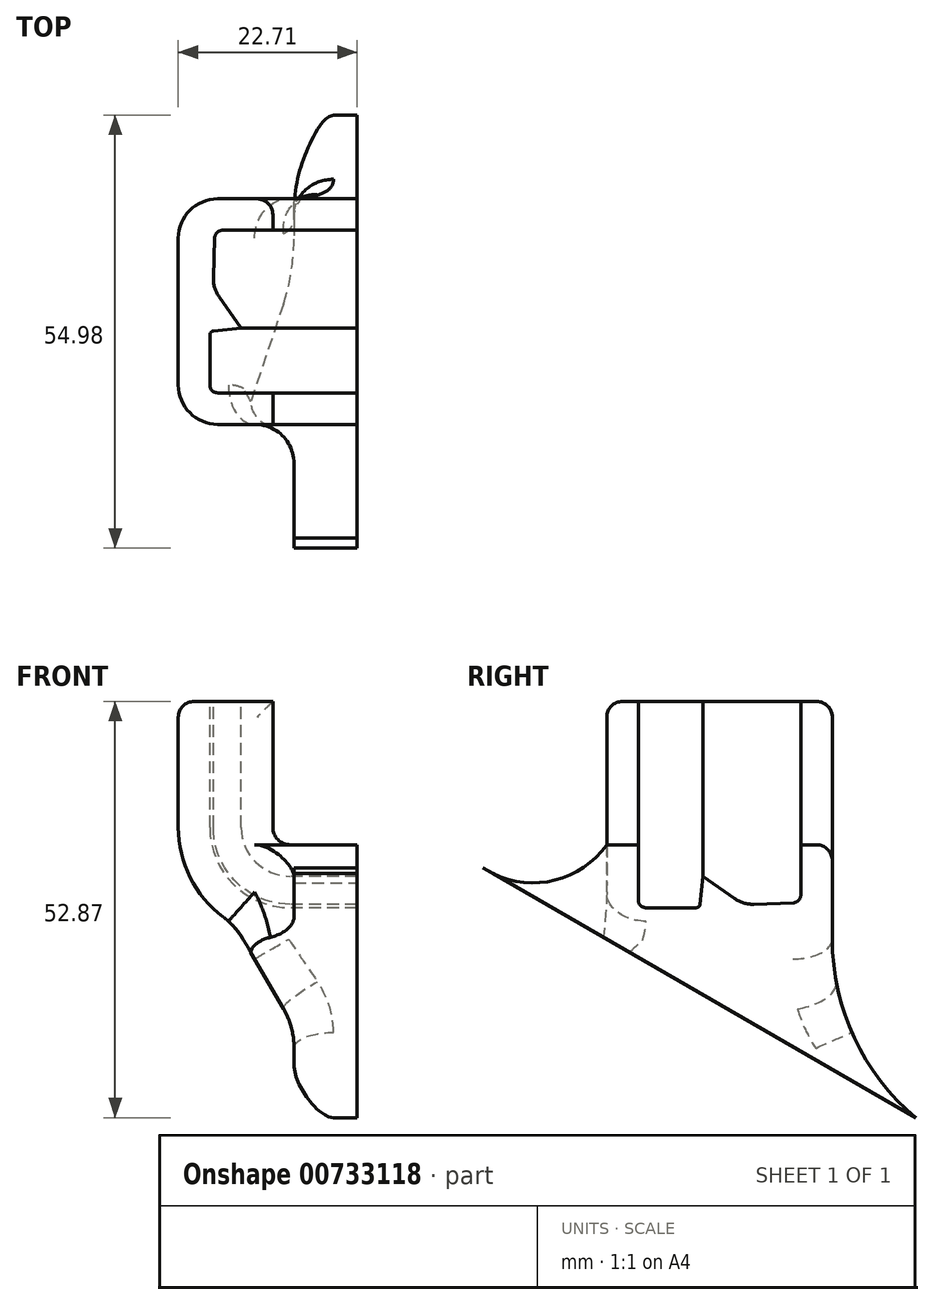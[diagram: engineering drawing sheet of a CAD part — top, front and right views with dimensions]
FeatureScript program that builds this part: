
annotation { "Feature Type Name" : "Feature", "Feature Type Description" : "" }
export const myFeature = defineFeature(function(context is Context, id is Id, definition is map)
    precondition{}
    {
        {
            var Q0;
            Q0=qCreatedBy(makeId("Front.planeOp"),FACE);
            var sketch = newSketch(context, id + "F0", { "sketchPlane" : qUnion([Q0])});
            skLineSegment(sketch, "E0", {"start": v(-73, 30.2) * mm, "end": v(-73, 14.2) * mm});
            skLineSegment(sketch, "E1", {"start": v(-58.8, 0) * mm, "end": v(0, 0) * mm});
            skPoint(sketch, "E2.visualSharp", {"position": v(-73, 0) * mm});
            skArc(sketch, "E2.filletArc", {"start": v(-73, 14.2) * mm, "mid": v(-68.84, 4.16) * mm, "end": v(-58.8, 0) * mm});
            skSolve(sketch);
        }
        {
            var Q0;
            Q0=qCreatedBy(makeId("Right.planeOp"),FACE);
            var sketch = newSketch(context, id + "F1", { "sketchPlane" : qUnion([Q0])});
            skLineSegment(sketch, "E3", {"start": v(0, 12) * mm, "end": v(4, 12) * mm});
            skLineSegment(sketch, "E4", {"start": v(4, 12) * mm, "end": v(4, 5) * mm});
            skLineSegment(sketch, "E5", {"start": v(5, 4) * mm, "end": v(11.35, 4) * mm});
            skLineSegment(sketch, "E6", {"start": v(11.85, 4.44) * mm, "end": v(12.25, 8) * mm});
            skLineSegment(sketch, "E7", {"start": v(24.65, 5.62) * mm, "end": v(24.65, 12) * mm});
            skLineSegment(sketch, "E8", {"start": v(24.65, 12) * mm, "end": v(28.65, 12) * mm});
            skLineSegment(sketch, "E9", {"start": v(28.65, 12) * mm, "end": v(28.65, 0) * mm});
            skLineSegment(sketch, "E10", {"start": v(28.65, 0) * mm, "end": v(0, 0) * mm});
            skLineSegment(sketch, "E11", {"start": v(0, 0) * mm, "end": v(0, 12) * mm});
            skLineSegment(sketch, "E12", {"start": v(12.25, 8) * mm, "end": v(16.21, 5.18) * mm});
            skPoint(sketch, "E13.visualSharp", {"position": v(16.59, 4.92) * mm});
            skPoint(sketch, "E14.visualSharp", {"position": v(4, 4) * mm});
            skArc(sketch, "E14.filletArc", {"start": v(4, 5) * mm, "mid": v(4.3, 4.3) * mm, "end": v(5, 4) * mm});
            skLineSegment(sketch, "E15", {"start": v(23.68, 4.62) * mm, "end": v(18.67, 4.45) * mm});
            skPoint(sketch, "E16.visualSharp", {"position": v(17.32, 4.4) * mm});
            skArc(sketch, "E16.filletArc", {"start": v(16.21, 5.18) * mm, "mid": v(17.38, 4.61) * mm, "end": v(18.67, 4.45) * mm});
            skPoint(sketch, "E17.visualSharp", {"position": v(24.65, 4.66) * mm});
            skArc(sketch, "E17.filletArc", {"start": v(23.68, 4.62) * mm, "mid": v(24.37, 4.93) * mm, "end": v(24.65, 5.62) * mm});
            skPoint(sketch, "E18.visualSharp", {"position": v(11.8, 4) * mm});
            skArc(sketch, "E18.filletArc", {"start": v(11.35, 4) * mm, "mid": v(11.69, 4.13) * mm, "end": v(11.85, 4.44) * mm});
            skSolve(sketch);
        }
        {
            var Q0;
            Q0 = qSketchRegion(id + "F1", true);
            var Q1;
            Q1 = qConstructionFilter(qBodyType(qCreatedBy(id + "F0" ,EDGE), BodyType.WIRE), ConstructionObject.NO);
            sweep(context, id + "F2", {"profiles" : qUnion([Q0]), "path" : qUnion([Q1])});
        }
        {
            var Q0;
            Q0=qCreatedBy(makeId("Top.planeOp"),FACE);
            var sketch = newSketch(context, id + "F3", { "sketchPlane" : qUnion([Q0])});
            skLineSegment(sketch, "E19.bottom", {"start": v(-50.3, -27.48) * mm, "end": v(2.48, -27.48) * mm});
            skLineSegment(sketch, "E19.top", {"start": v(-50.3, 55.65) * mm, "end": v(2.48, 55.65) * mm});
            skLineSegment(sketch, "E19.left", {"start": v(2.48, -27.48) * mm, "end": v(2.48, 55.65) * mm});
            skLineSegment(sketch, "E19.right", {"start": v(-50.3, -27.48) * mm, "end": v(-50.3, 55.65) * mm});
            skSolve(sketch);
        }
        {
            var Q0;
            Q0 = qSketchRegion(id + "F3", true);
            extrude(context, id + "F4", {"entities" : qUnion([Q0]), "operationType" : NewBodyOperationType.REMOVE, "depth" : 25 * mm, "offsetDistance" : 25 * mm});
        }
        {
            var Q0;
            Q0=makeQuery(id+"F4.boolean.opBoolean","COPY",FACE,{"derivedFrom":makeQuery(id+"F4.opExtrude","SWEPT_FACE",FACE,{"disambiguationData":[OSD([sQuery(id+"F3.wireOp",EDGE,"E19.right")])]})});
            var sketch = newSketch(context, id + "F5", { "sketchPlane" : qUnion([Q0])});
            skLineSegment(sketch, "E20", {"start": v(0, 0) * mm, "end": v(-15.7, 9.07) * mm});
            skLineSegment(sketch, "E21", {"start": v(0, 0) * mm, "end": v(39.27, -22.67) * mm});
            skArc(sketch, "E22", {"start": v(28.65, 0) * mm, "mid": v(31.44, -12.52) * mm, "end": v(39.27, -22.67) * mm});
            skArc(sketch, "E23", {"start": v(-15.7, 9.07) * mm, "mid": v(-7.26, 7.35) * mm, "end": v(0, 12) * mm});
            skPoint(sketch, "E23.second.point", {"position": v(0, 12) * mm});
            skPoint(sketch, "E23.third.point", {"position": v(-15.7, 28.17) * mm});
            skLineSegment(sketch, "E24", {"start": v(28.65, 0) * mm, "end": v(3.33, 0) * mm});
            skLineSegment(sketch, "E25", {"start": v(3.33, 0) * mm, "end": v(0, 12) * mm});
            skSolve(sketch);
        }
        {
            var Q0;
            Q0 = qSketchRegion(id + "F5", true);
            var Q1;
            Q1=makeQuery(id+"F2.opSweep","SWEPT_FACE",FACE,{"disambiguationData":[OSD([sQuery(id+"F0.wireOp",EDGE,"E1"),sQuery(id+"F1.wireOp",EDGE,"E3")])]});
            extrude(context, id + "F6", {"entities" : qUnion([Q0]), "operationType" : NewBodyOperationType.ADD, "oppositeDirection" : true, "depth" : 8 * mm, "endBoundEntityFace" : qUnion([Q1]), "offsetDistance" : 25 * mm});
        }
        {
            var Q0;
            Q0=makeQuery(id+"F6.boolean.opBoolean","INTERSECT",EDGE,{"derivedFrom":[makeQuery(id+"F2.opSweep","SWEPT_FACE",FACE,{"disambiguationData":[OSD([sQuery(id+"F0.wireOp",EDGE,"E1"),sQuery(id+"F1.wireOp",EDGE,"E10")])]}),makeQuery(id+"F6.opExtrude","CAP_FACE",FACE,{"disambiguationData":[OSD([sQuery(id+"F5.wireOp",EDGE,"E20"),sQuery(id+"F5.wireOp",EDGE,"E21"),sQuery(id+"F5.wireOp",EDGE,"E22"),sQuery(id+"F5.wireOp",EDGE,"E23"),sQuery(id+"F5.wireOp",EDGE,"E24"),sQuery(id+"F5.wireOp",EDGE,"E25")])],"isStart":false})]});
            chamfer(context, id + "F7", {"entities" : qUnion([Q0]), "width" : 15 * mm, "tangentPropagation" : true});
        }
        {
            var Q0;
            {var subQ0=sQuery(id+"F5.wireOp",EDGE,"E21");var subQ1=sQuery(id+"F5.wireOp",EDGE,"E20");var subQ2=sQuery(id+"F0.wireOp",EDGE,"E1");var subQ3=makeQuery(id+"F2.opSweep","SWEPT_FACE",FACE,{"disambiguationData":[OSD([subQ2,sQuery(id+"F1.wireOp",EDGE,"E10")])]});var subQ4=sQuery(id+"F5.wireOp",EDGE,"E22");var subQ5=makeQuery(id+"F6.opExtrude","CAP_FACE",FACE,{"disambiguationData":[OSD([subQ1,subQ0,subQ4,sQuery(id+"F5.wireOp",EDGE,"E23"),sQuery(id+"F5.wireOp",EDGE,"E24"),sQuery(id+"F5.wireOp",EDGE,"E25")])],"isStart":false});Q0=makeQuery(id+"F7.opChamfer","BLEND_EDGE",EDGE,{"blendedFrom":[makeQuery(id+"F6.boolean.opBoolean","INTERSECT",EDGE,{"derivedFrom":[subQ3,subQ5]}),makeQuery(id+"F6.boolean.opBoolean","SPLIT",FACE,{"disambiguationData":[TD([makeQuery(id+"F6.opExtrude","SWEPT_FACE",FACE,{"disambiguationData":[OSD([subQ4])]})])],"derivedFrom":subQ5})],"blendedInto":[makeQuery(id+"F6.boolean.opBoolean","SPLIT",FACE,{"disambiguationData":[TD([makeQuery(id+"F6.opExtrude","SWEPT_FACE",FACE,{"disambiguationData":[OSD([subQ4])]})])],"derivedFrom":subQ5})]});}
            var Q1;
            {var subQ0=sQuery(id+"F1.wireOp",EDGE,"E10");Q1=makeQuery(id+"F7.opChamfer","BLEND_EDGE",EDGE,{"blendedFrom":[makeQuery(id+"F6.boolean.opBoolean","INTERSECT",EDGE,{"derivedFrom":[makeQuery(id+"F2.opSweep","SWEPT_FACE",FACE,{"disambiguationData":[OSD([sQuery(id+"F0.wireOp",EDGE,"E1"),subQ0])]}),makeQuery(id+"F6.opExtrude","CAP_FACE",FACE,{"disambiguationData":[OSD([sQuery(id+"F5.wireOp",EDGE,"E20"),sQuery(id+"F5.wireOp",EDGE,"E21"),sQuery(id+"F5.wireOp",EDGE,"E22"),sQuery(id+"F5.wireOp",EDGE,"E23"),sQuery(id+"F5.wireOp",EDGE,"E24"),sQuery(id+"F5.wireOp",EDGE,"E25")])],"isStart":false})]}),makeQuery(id+"F2.opSweep","SWEPT_FACE",FACE,{"disambiguationData":[OSD([sQuery(id+"F0.wireOp",EDGE,"E2.filletArc"),subQ0])]})],"blendedInto":[makeQuery(id+"F2.opSweep","SWEPT_FACE",FACE,{"disambiguationData":[OSD([sQuery(id+"F0.wireOp",EDGE,"E2.filletArc"),subQ0])]})]});}
            fillet(context, id + "F8", {"entities" : qUnion([Q0, Q1]), "radius" : 10 * mm, "tangentPropagation" : true, "allowEdgeOverflow" : false});
        }
        {
            var Q0;
            Q0=makeQuery(id+"F6.boolean.opBoolean","INTERSECT",EDGE,{"derivedFrom":[makeQuery(id+"F2.opSweep","SWEPT_FACE",FACE,{"disambiguationData":[OSD([sQuery(id+"F0.wireOp",EDGE,"E1"),sQuery(id+"F1.wireOp",EDGE,"E11")])]}),makeQuery(id+"F6.opExtrude","CAP_FACE",FACE,{"disambiguationData":[OSD([sQuery(id+"F5.wireOp",EDGE,"E20"),sQuery(id+"F5.wireOp",EDGE,"E21"),sQuery(id+"F5.wireOp",EDGE,"E22"),sQuery(id+"F5.wireOp",EDGE,"E23"),sQuery(id+"F5.wireOp",EDGE,"E24"),sQuery(id+"F5.wireOp",EDGE,"E25")])],"isStart":false})]});
            fillet(context, id + "F9", {"entities" : qUnion([Q0]), "radius" : 5 * mm, "tangentPropagation" : true, "allowEdgeOverflow" : false});
        }
        {
            var Q0;
            Q0=makeQuery(id+"F2.opSweep","SWEPT_EDGE",EDGE,{"disambiguationData":[OSD([sQuery(id+"F0.wireOp",EDGE,"E0"),sQuery(id+"F1.wireOp",EDGE,"E10"),sQuery(id+"F1.wireOp",EDGE,"E11")])]});
            var Q1;
            Q1=makeQuery(id+"F2.opSweep","SWEPT_EDGE",EDGE,{"disambiguationData":[OSD([sQuery(id+"F0.wireOp",EDGE,"E0"),sQuery(id+"F1.wireOp",EDGE,"E9"),sQuery(id+"F1.wireOp",EDGE,"E10")])]});
            fillet(context, id + "F10", {"entities" : qUnion([Q0, Q1]), "radius" : 5 * mm, "tangentPropagation" : true, "allowEdgeOverflow" : false});
        }
        {
            var Q0;
            Q0=makeQuery(id+"F2.opSweep","SWEPT_EDGE",EDGE,{"disambiguationData":[OSD([sQuery(id+"F0.wireOp",EDGE,"E0"),sQuery(id+"F1.wireOp",EDGE,"E8"),sQuery(id+"F1.wireOp",EDGE,"E9")])]});
            var Q1;
            Q1=makeQuery(id+"F2.opSweep","CAP_EDGE",EDGE,{"disambiguationData":[OSD([sQuery(id+"F0.wireOp",VERTEX,"E0.start"),sQuery(id+"F1.wireOp",EDGE,"E11")])],"isStart":false});
            fillet(context, id + "F11", {"entities" : qUnion([Q0, Q1]), "radius" : 2 * mm, "tangentPropagation" : true, "allowEdgeOverflow" : false});
        }
    });
